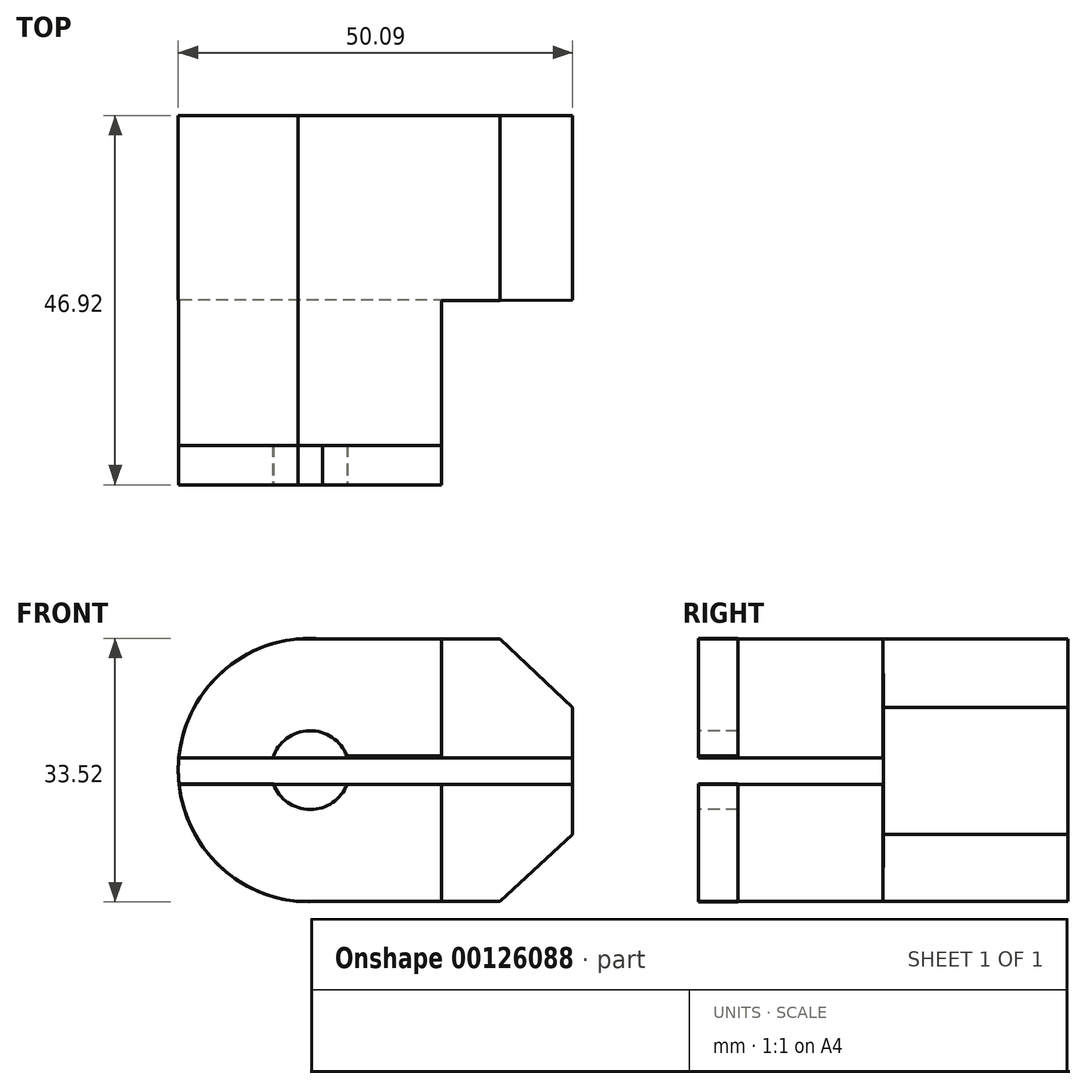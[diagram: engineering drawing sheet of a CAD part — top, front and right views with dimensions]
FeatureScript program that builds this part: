
annotation { "Feature Type Name" : "Feature", "Feature Type Description" : "" }
export const myFeature = defineFeature(function(context is Context, id is Id, definition is map)
    precondition{}
    {
        {
            var Q0;
            Q0=qCreatedBy(makeId("Front.planeOp"),FACE);
            var sketch = newSketch(context, id + "F0", { "sketchPlane" : qUnion([Q0])});
            skCircle(sketch, "E0", {"center": v(0, 0) * mm, "radius": 5 * mm});
            skLineSegment(sketch, "E1", {"start": v(0, 16.69) * mm, "end": v(24.11, 16.69) * mm});
            skLineSegment(sketch, "E2", {"start": v(24.11, 16.69) * mm, "end": v(33.33, 7.97) * mm});
            skLineSegment(sketch, "E3", {"start": v(33.33, 7.97) * mm, "end": v(33.33, -8.17) * mm});
            skLineSegment(sketch, "E4", {"start": v(33.33, -8.17) * mm, "end": v(24.11, -16.69) * mm});
            skLineSegment(sketch, "E5", {"start": v(24.11, -16.69) * mm, "end": v(0, -16.69) * mm});
            skLineSegment(sketch, "E6", {"start": v(-16.69, 1.55) * mm, "end": v(-4.76, 1.55) * mm});
            skLineSegment(sketch, "E7", {"start": v(-4.68, -1.75) * mm, "end": v(-16.67, -1.75) * mm});
            skLineSegment(sketch, "E8", {"start": v(4.67, 1.79) * mm, "end": v(33.33, 1.79) * mm});
            skLineSegment(sketch, "E9", {"start": v(4.67, -1.79) * mm, "end": v(33.33, -1.79) * mm});
            skArc(sketch, "E10", {"start": v(16.66, 1.79) * mm, "mid": v(-16.76, 0) * mm, "end": v(16.66, -1.79) * mm});
            skSolve(sketch);
        }
        {
            var Q0;
            Q0=qCreatedBy(makeId("Top.planeOp"),FACE);
            var sketch = newSketch(context, id + "F1", { "sketchPlane" : qUnion([Q0])});
            skLineSegment(sketch, "E11", {"start": v(-30.57, 0) * mm, "end": v(-30.57, 46.92) * mm, "construction": true});
            skLineSegment(sketch, "E12", {"start": v(-30.57, 46.92) * mm, "end": v(33.33, 46.92) * mm, "construction": true});
            skLineSegment(sketch, "E13", {"start": v(33.33, 46.92) * mm, "end": v(33.33, 31.28) * mm, "construction": true});
            skLineSegment(sketch, "E14", {"start": v(0, 0) * mm, "end": v(-30.57, 0) * mm, "construction": true});
            skLineSegment(sketch, "E15", {"start": v(33.33, 31.28) * mm, "end": v(16.66, 31.28) * mm, "construction": true});
            skLineSegment(sketch, "E16", {"start": v(16.66, 0) * mm, "end": v(0, 0) * mm, "construction": true});
            skLineSegment(sketch, "E17", {"start": v(24.11, 46.92) * mm, "end": v(24.11, 31.28) * mm, "construction": true});
            skLineSegment(sketch, "E18", {"start": v(-4.68, 0) * mm, "end": v(-4.68, 46.92) * mm, "construction": true});
            skLineSegment(sketch, "E19", {"start": v(4.67, 0) * mm, "end": v(4.67, 46.92) * mm, "construction": true});
            skLineSegment(sketch, "E20", {"start": v(-30.57, 23.46) * mm, "end": v(-4.68, 23.46) * mm, "construction": true});
            skLineSegment(sketch, "E21", {"start": v(16.66, 31.38) * mm, "end": v(16.66, 0) * mm, "construction": true});
            skLineSegment(sketch, "E22", {"start": v(33.33, 23.46) * mm, "end": v(4.67, 23.35) * mm, "construction": true});
            skPoint(sketch, "E22.endSnap0", {"position": v(4.67, 23.46) * mm});
            skLineSegment(sketch, "E23", {"start": v(16.66, 0) * mm, "end": v(33.33, 0) * mm});
            skLineSegment(sketch, "E24", {"start": v(33.33, 0) * mm, "end": v(33.33, 23.46) * mm});
            skLineSegment(sketch, "E25", {"start": v(16.66, 23.4) * mm, "end": v(16.66, 0) * mm});
            skLineSegment(sketch, "E26", {"start": v(16.66, 23.4) * mm, "end": v(33.33, 23.46) * mm});
            skSolve(sketch);
        }
        {
            var Q0;
            Q0=qCreatedBy(makeId("Right.planeOp"),FACE);
            var sketch = newSketch(context, id + "F2", { "sketchPlane" : qUnion([Q0])});
            skLineSegment(sketch, "E27", {"start": v(0, 16.69) * mm, "end": v(46.92, 16.69) * mm});
            skLineSegment(sketch, "E28", {"start": v(46.92, 16.69) * mm, "end": v(46.92, -16.69) * mm});
            skLineSegment(sketch, "E29", {"start": v(46.92, -16.69) * mm, "end": v(0, -16.69) * mm});
            skLineSegment(sketch, "E30", {"start": v(0, -16.69) * mm, "end": v(0, -1.79) * mm});
            skLineSegment(sketch, "E31", {"start": v(0, -1.79) * mm, "end": v(23.46, -1.79) * mm});
            skLineSegment(sketch, "E32", {"start": v(23.46, -1.79) * mm, "end": v(23.46, 1.55) * mm});
            skLineSegment(sketch, "E33", {"start": v(23.46, 1.55) * mm, "end": v(0, 1.55) * mm});
            skLineSegment(sketch, "E34", {"start": v(0, 1.55) * mm, "end": v(0, 16.69) * mm});
            skLineSegment(sketch, "E35", {"start": v(12.02, 16.69) * mm, "end": v(12.02, 1.55) * mm});
            skLineSegment(sketch, "E36.trimOffspring", {"start": v(12.02, -1.79) * mm, "end": v(12.02, -16.69) * mm});
            skLineSegment(sketch, "E37", {"start": v(12.02, 7.97) * mm, "end": v(46.92, 7.97) * mm});
            skLineSegment(sketch, "E38", {"start": v(12.02, -8.17) * mm, "end": v(46.92, -8.17) * mm});
            skLineSegment(sketch, "E39", {"start": v(12.02, 7.97) * mm, "end": v(0, 7.97) * mm, "construction": true});
            skLineSegment(sketch, "E40", {"start": v(12.02, -8.17) * mm, "end": v(0, -8.17) * mm, "construction": true});
            skLineSegment(sketch, "E41", {"start": v(0, 0) * mm, "end": v(46.92, 0) * mm, "construction": true});
            skSolve(sketch);
        }
        {
            var Q0;
            Q0 = qSketchRegion(id + "F0", true);
            extrude(context, id + "F3", {"entities" : qUnion([Q0]), "oppositeDirection" : true, "depth" : 5 * mm});
        }
        {
            var Q0;
            Q0=qCreatedBy(makeId("Front.planeOp"),FACE);
            var sketch = newSketch(context, id + "F4", { "sketchPlane" : qUnion([Q0])});
            skLineSegment(sketch, "E42", {"start": v(4.67, 1.79) * mm, "end": v(33.33, 1.79) * mm});
            skLineSegment(sketch, "E43", {"start": v(33.33, 1.79) * mm, "end": v(33.33, -1.79) * mm});
            skLineSegment(sketch, "E44", {"start": v(33.33, -1.79) * mm, "end": v(4.67, -1.79) * mm});
            skArc(sketch, "E45", {"start": v(-4.76, 1.55) * mm, "mid": v(-5, -0.1) * mm, "end": v(-4.68, -1.75) * mm});
            skLineSegment(sketch, "E46", {"start": v(-4.76, 1.55) * mm, "end": v(-16.68, 1.55) * mm});
            skLineSegment(sketch, "E47", {"start": v(-16.68, -1.75) * mm, "end": v(-4.68, -1.75) * mm});
            skArc(sketch, "E48", {"start": v(-16.68, 1.55) * mm, "mid": v(-16.75, -0.1) * mm, "end": v(-16.66, -1.75) * mm});
            skArc(sketch, "E49.trimOffspring", {"start": v(4.67, -1.79) * mm, "mid": v(5, 0) * mm, "end": v(4.67, 1.79) * mm});
            skLineSegment(sketch, "E50", {"start": v(33.33, -1.79) * mm, "end": v(33.33, -8.17) * mm});
            skSolve(sketch);
        }
        {
            var Q0;
            Q0 = qSketchRegion(id + "F2", true);
            var Q1;
            Q1=makeQuery(id+"F3.opExtrude","SWEPT_FACE",FACE,{"disambiguationData":[OSD([sQuery(id+"F0.wireOp",EDGE,"E3")])]});
            var Q2;
            {var subQ0=sQuery(id+"F0.wireOp",EDGE,"E10");var subQ5=sQuery(id+"F0.wireOp",EDGE,"E1");Q2=makeQuery(id+"F6.boolean.opBoolean","SPLIT",FACE,{"disambiguationData":[TD([makeQuery(id+"F3.opExtrude","SWEPT_FACE",FACE,{"disambiguationData":[OSD([subQ5])]})])],"derivedFrom":makeQuery(id+"F3.opExtrude","SWEPT_FACE",FACE,{"disambiguationData":[OSD([subQ0])]})});}
            extrude(context, id + "F5", {"entities" : qUnion([Q0]), "endBound" : BoundingType.UP_TO_SURFACE, "endBoundEntityFace" : qUnion([Q1]), "depth" : 25 * mm, "hasSecondDirection" : true, "secondDirectionBound" : SecondDirectionBoundingType.UP_TO_SURFACE, "secondDirectionOppositeDirection" : true, "secondDirectionBoundEntityFace" : qUnion([Q2]), "secondDirectionDepth" : 25 * mm});
        }
        {
            var Q0;
            Q0 = qSketchRegion(id + "F4", true);
            extrude(context, id + "F6", {"entities" : qUnion([Q0]), "operationType" : NewBodyOperationType.REMOVE, "oppositeDirection" : true, "depth" : 5 * mm});
        }
        {
            var Q0;
            Q0=qCreatedBy(makeId("Front.planeOp"),FACE);
            var sketch = newSketch(context, id + "F7", { "sketchPlane" : qUnion([Q0])});
            skLineSegment(sketch, "E51", {"start": v(33.33, 1.79) * mm, "end": v(33.33, -1.79) * mm});
            skLineSegment(sketch, "E52", {"start": v(33.33, -1.79) * mm, "end": v(33.33, -8.17) * mm});
            skLineSegment(sketch, "E53", {"start": v(33.33, -8.17) * mm, "end": v(24.11, -16.69) * mm});
            skLineSegment(sketch, "E54", {"start": v(24.11, -16.69) * mm, "end": v(33.33, -16.69) * mm});
            skLineSegment(sketch, "E55", {"start": v(33.33, -16.69) * mm, "end": v(33.33, 16.69) * mm});
            skLineSegment(sketch, "E56", {"start": v(33.33, 16.69) * mm, "end": v(24.11, 16.69) * mm});
            skLineSegment(sketch, "E57", {"start": v(24.11, 16.69) * mm, "end": v(33.33, 7.97) * mm});
            skSolve(sketch);
        }
        {
            var Q0;
            Q0 = qSketchRegion(id + "F1", true);
            var Q1;
            Q1=makeQuery(id+"F3.opExtrude","SWEPT_FACE",FACE,{"disambiguationData":[OSD([sQuery(id+"F0.wireOp",EDGE,"E1")])]});
            var Q2;
            Q2=makeQuery(id+"F3.opExtrude","SWEPT_FACE",FACE,{"disambiguationData":[OSD([sQuery(id+"F0.wireOp",EDGE,"E5")])]});
            extrude(context, id + "F8", {"entities" : qUnion([Q0]), "operationType" : NewBodyOperationType.REMOVE, "endBound" : BoundingType.UP_TO_SURFACE, "endBoundEntityFace" : qUnion([Q1]), "depth" : 25 * mm, "hasSecondDirection" : true, "secondDirectionBound" : SecondDirectionBoundingType.UP_TO_SURFACE, "secondDirectionOppositeDirection" : true, "secondDirectionBoundEntityFace" : qUnion([Q2]), "secondDirectionDepth" : 25 * mm});
        }
        {
            var Q0;
            Q0 = qSketchRegion(id + "F7", true);
            extrude(context, id + "F9", {"entities" : qUnion([Q0]), "operationType" : NewBodyOperationType.REMOVE, "endBound" : BoundingType.THROUGH_ALL, "oppositeDirection" : true, "depth" : 25 * mm});
        }
    });
